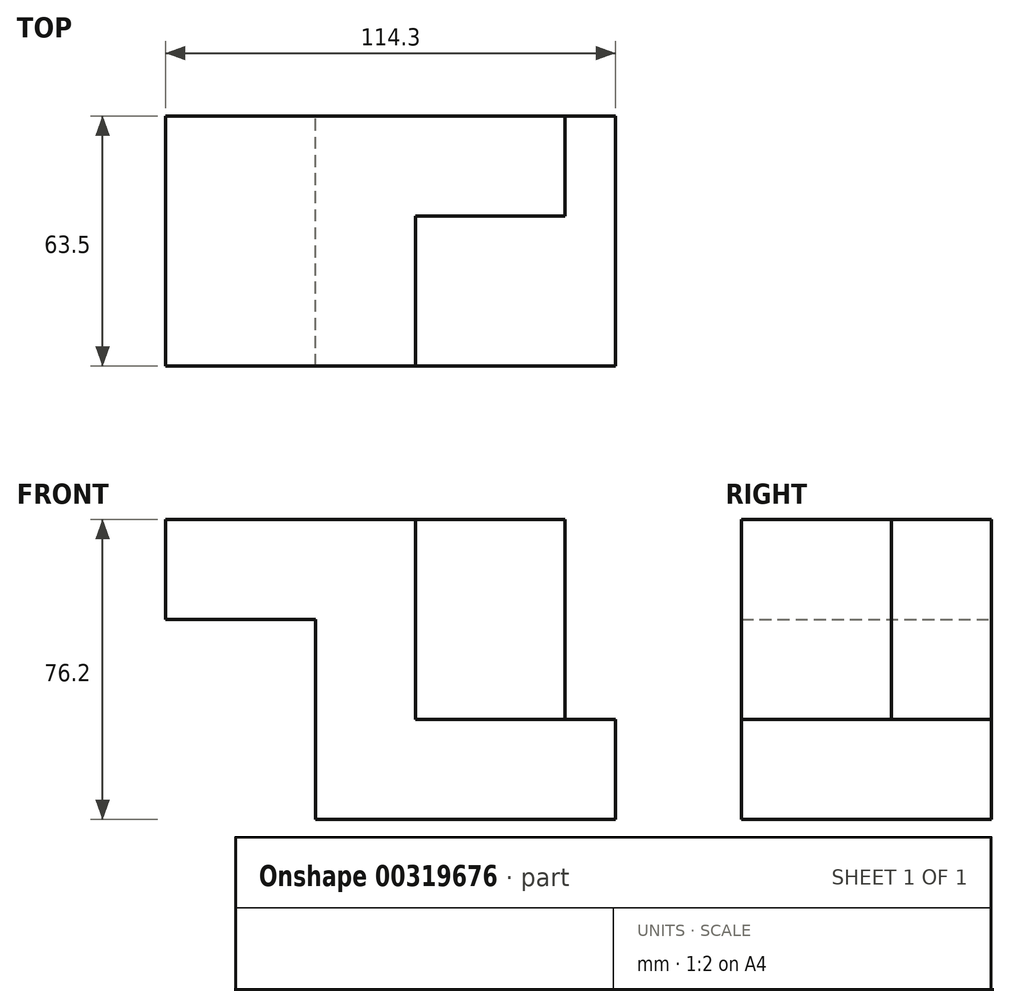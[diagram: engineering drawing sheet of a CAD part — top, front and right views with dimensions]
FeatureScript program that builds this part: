
annotation { "Feature Type Name" : "Feature", "Feature Type Description" : "" }
export const myFeature = defineFeature(function(context is Context, id is Id, definition is map)
    precondition{}
    {
        {
            var Q0;
            Q0=qCreatedBy(makeId("Front.planeOp"),FACE);
            var sketch = newSketch(context, id + "F0", { "sketchPlane" : qUnion([Q0])});
            skLineSegment(sketch, "E0", {"start": v(-25.3, -50.8) * mm, "end": v(50.9, -50.8) * mm});
            skLineSegment(sketch, "E1", {"start": v(50.9, -50.8) * mm, "end": v(50.9, -25.4) * mm});
            skLineSegment(sketch, "E2", {"start": v(50.9, -25.4) * mm, "end": v(0.1, -25.4) * mm});
            skLineSegment(sketch, "E3", {"start": v(0.1, -25.4) * mm, "end": v(0.1, 25.4) * mm});
            skLineSegment(sketch, "E4", {"start": v(0.1, 25.4) * mm, "end": v(-63.4, 25.4) * mm});
            skLineSegment(sketch, "E5", {"start": v(-63.4, 25.4) * mm, "end": v(-63.4, 0) * mm});
            skLineSegment(sketch, "E6", {"start": v(-63.4, 0) * mm, "end": v(-25.3, 0) * mm});
            skLineSegment(sketch, "E7", {"start": v(-25.3, 0) * mm, "end": v(-25.3, -50.8) * mm});
            skSolve(sketch);
        }
        {
            var Q0;
            Q0=makeQuery(id+"F0.imprint","IMPRINT",FACE,{"disambiguationData":[TD([[makeQuery(id+"F0.imprint","IMPRINT",EDGE,{"derivedFrom":sQuery(id+"F0.wireOp",EDGE,"E0")}),1.0]])]});
            extrude(context, id + "F1", {"entities" : qUnion([Q0]), "depth" : 63.5 * mm});
        }
        {
            var Q0;
            Q0=makeQuery(id+"F1.opExtrude","SWEPT_FACE",FACE,{"disambiguationData":[OSD([sQuery(id+"F0.wireOp",EDGE,"E4")])]});
            var sketch = newSketch(context, id + "F2", { "sketchPlane" : qUnion([Q0])});
            skLineSegment(sketch, "E8", {"start": v(0, 0) * mm, "end": v(38.1, 0) * mm});
            skLineSegment(sketch, "E9", {"start": v(38.1, 0) * mm, "end": v(38.1, -25.4) * mm});
            skLineSegment(sketch, "E10", {"start": v(38.1, -25.4) * mm, "end": v(0.1, -25.4) * mm});
            skLineSegment(sketch, "E11", {"start": v(0.1, -25.4) * mm, "end": v(0.1, 0) * mm});
            skSolve(sketch);
        }
        {
            var Q0;
            {var subQ2=sQuery(id+"F2.wireOp",EDGE,"E9");Q0=makeQuery(id+"F2.imprint","IMPRINT",FACE,{"disambiguationData":[TD([[makeQuery(id+"F2.imprint","IMPRINT",EDGE,{"derivedFrom":subQ2}),-1.0]])]});}
            extrude(context, id + "F3", {"entities" : qUnion([Q0]), "operationType" : NewBodyOperationType.ADD, "oppositeDirection" : true, "depth" : 50.8 * mm});
        }
    });
